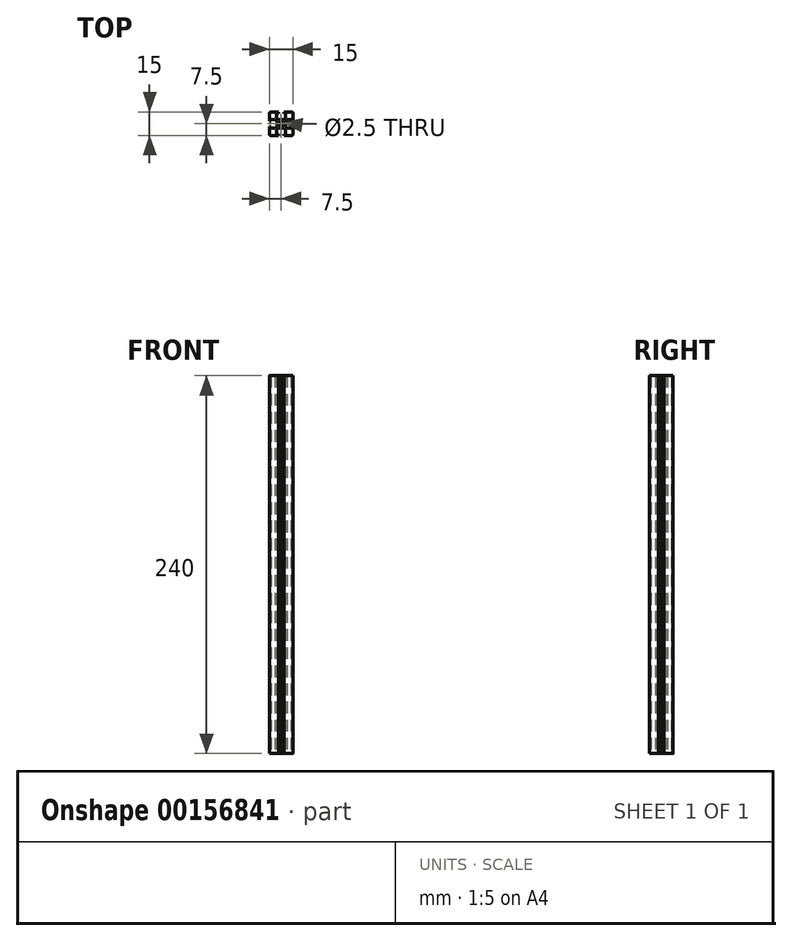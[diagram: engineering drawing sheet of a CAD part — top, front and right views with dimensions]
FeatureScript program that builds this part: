
annotation { "Feature Type Name" : "Feature", "Feature Type Description" : "" }
export const myFeature = defineFeature(function(context is Context, id is Id, definition is map)
    precondition{}
    {
        {
            var Q0;
            Q0=qCreatedBy(makeId("Top.planeOp"),FACE);
            var sketch = newSketch(context, id + "F0", { "sketchPlane" : qUnion([Q0])});
            skLineSegment(sketch, "E0.bottom", {"start": v(6.5, -7.5) * mm, "end": v(1.7, -7.5) * mm});
            skLineSegment(sketch, "E0.top", {"start": v(6.5, 7.5) * mm, "end": v(1.7, 7.5) * mm});
            skLineSegment(sketch, "E0.left", {"start": v(7.5, -6.5) * mm, "end": v(7.5, -1.7) * mm});
            skLineSegment(sketch, "E0.right", {"start": v(-7.5, -6.5) * mm, "end": v(-7.5, -1.7) * mm});
            skPoint(sketch, "E0.middle", {"position": v(0, 0) * mm});
            skPoint(sketch, "E1.visualSharp", {"position": v(7.5, 7.5) * mm});
            skArc(sketch, "E1.filletArc", {"start": v(7.5, 6.5) * mm, "mid": v(7.2, 7.2) * mm, "end": v(6.5, 7.5) * mm});
            skPoint(sketch, "E2.visualSharp", {"position": v(-7.5, 7.5) * mm});
            skArc(sketch, "E2.filletArc", {"start": v(-6.5, 7.5) * mm, "mid": v(-7.2, 7.2) * mm, "end": v(-7.5, 6.5) * mm});
            skPoint(sketch, "E3.visualSharp", {"position": v(-7.5, -7.5) * mm});
            skArc(sketch, "E3.filletArc", {"start": v(-7.5, -6.5) * mm, "mid": v(-7.2, -7.2) * mm, "end": v(-6.5, -7.5) * mm});
            skPoint(sketch, "E4.visualSharp", {"position": v(7.5, -7.5) * mm});
            skArc(sketch, "E4.filletArc", {"start": v(6.5, -7.5) * mm, "mid": v(7.2, -7.2) * mm, "end": v(7.5, -6.5) * mm});
            skCircle(sketch, "E5", {"center": v(0, 0) * mm, "radius": 1.25 * mm});
            skLineSegment(sketch, "E6", {"start": v(-1.7, 7.5) * mm, "end": v(-1.7, 6.4) * mm});
            skLineSegment(sketch, "E7", {"start": v(-1.7, 6.4) * mm, "end": v(-2.85, 6.4) * mm});
            skLineSegment(sketch, "E8", {"start": v(-2.85, 6.4) * mm, "end": v(-2.85, 3.8) * mm});
            skLineSegment(sketch, "E9", {"start": v(-2.85, 3.8) * mm, "end": v(-1.7, 2.8) * mm});
            skLineSegment(sketch, "E10", {"start": v(-1.7, 2.8) * mm, "end": v(-0.52, 2.8) * mm});
            skLineSegment(sketch, "E11", {"start": v(-0.52, 2.8) * mm, "end": v(0, 2.5) * mm});
            skLineSegment(sketch, "E12", {"start": v(0, 7.5) * mm, "end": v(0, 1.25) * mm, "construction": true});
            skLineSegment(sketch, "E13.MirrorCS", {"start": v(1.7, 7.5) * mm, "end": v(1.7, 6.4) * mm});
            skLineSegment(sketch, "E14.MirrorCS", {"start": v(1.7, 6.4) * mm, "end": v(2.85, 6.4) * mm});
            skLineSegment(sketch, "E15.MirrorCS", {"start": v(2.85, 6.4) * mm, "end": v(2.85, 3.8) * mm});
            skLineSegment(sketch, "E16.MirrorCS", {"start": v(2.85, 3.8) * mm, "end": v(1.7, 2.8) * mm});
            skLineSegment(sketch, "E17.MirrorCS", {"start": v(1.7, 2.8) * mm, "end": v(0.52, 2.8) * mm});
            skLineSegment(sketch, "E18.MirrorCS", {"start": v(0.52, 2.8) * mm, "end": v(0, 2.5) * mm});
            skLineSegment(sketch, "E19.1.0", {"start": v(-7.5, -1.7) * mm, "end": v(-6.4, -1.7) * mm});
            skLineSegment(sketch, "E19.1.1", {"start": v(-6.4, -1.7) * mm, "end": v(-6.4, -2.85) * mm});
            skLineSegment(sketch, "E19.1.2", {"start": v(-6.4, -2.85) * mm, "end": v(-3.8, -2.85) * mm});
            skLineSegment(sketch, "E19.1.3", {"start": v(-3.8, -2.85) * mm, "end": v(-2.8, -1.7) * mm});
            skLineSegment(sketch, "E19.1.4", {"start": v(-2.8, -1.7) * mm, "end": v(-2.8, -0.52) * mm});
            skLineSegment(sketch, "E19.1.5", {"start": v(-7.5, 1.7) * mm, "end": v(-6.4, 1.7) * mm});
            skLineSegment(sketch, "E19.1.6", {"start": v(-6.4, 1.7) * mm, "end": v(-6.4, 2.85) * mm});
            skLineSegment(sketch, "E19.1.7", {"start": v(-6.4, 2.85) * mm, "end": v(-3.8, 2.85) * mm});
            skLineSegment(sketch, "E19.1.8", {"start": v(-3.8, 2.85) * mm, "end": v(-2.8, 1.7) * mm});
            skLineSegment(sketch, "E19.1.9", {"start": v(-2.8, 1.7) * mm, "end": v(-2.8, 0.52) * mm});
            skLineSegment(sketch, "E19.1.10", {"start": v(-2.8, 0.52) * mm, "end": v(-2.5, 0) * mm});
            skLineSegment(sketch, "E19.1.11", {"start": v(-2.8, -0.52) * mm, "end": v(-2.5, 0) * mm});
            skLineSegment(sketch, "E19.2.0", {"start": v(1.7, -7.5) * mm, "end": v(1.7, -6.4) * mm});
            skLineSegment(sketch, "E19.2.1", {"start": v(1.7, -6.4) * mm, "end": v(2.85, -6.4) * mm});
            skLineSegment(sketch, "E19.2.2", {"start": v(2.85, -6.4) * mm, "end": v(2.85, -3.8) * mm});
            skLineSegment(sketch, "E19.2.3", {"start": v(2.85, -3.8) * mm, "end": v(1.7, -2.8) * mm});
            skLineSegment(sketch, "E19.2.4", {"start": v(1.7, -2.8) * mm, "end": v(0.52, -2.8) * mm});
            skLineSegment(sketch, "E19.2.5", {"start": v(-1.7, -7.5) * mm, "end": v(-1.7, -6.4) * mm});
            skLineSegment(sketch, "E19.2.6", {"start": v(-1.7, -6.4) * mm, "end": v(-2.85, -6.4) * mm});
            skLineSegment(sketch, "E19.2.7", {"start": v(-2.85, -6.4) * mm, "end": v(-2.85, -3.8) * mm});
            skLineSegment(sketch, "E19.2.8", {"start": v(-2.85, -3.8) * mm, "end": v(-1.7, -2.8) * mm});
            skLineSegment(sketch, "E19.2.9", {"start": v(-1.7, -2.8) * mm, "end": v(-0.52, -2.8) * mm});
            skLineSegment(sketch, "E19.2.10", {"start": v(-0.52, -2.8) * mm, "end": v(0, -2.5) * mm});
            skLineSegment(sketch, "E19.2.11", {"start": v(0.52, -2.8) * mm, "end": v(0, -2.5) * mm});
            skLineSegment(sketch, "E19.3.0", {"start": v(7.5, 1.7) * mm, "end": v(6.4, 1.7) * mm});
            skLineSegment(sketch, "E19.3.1", {"start": v(6.4, 1.7) * mm, "end": v(6.4, 2.85) * mm});
            skLineSegment(sketch, "E19.3.2", {"start": v(6.4, 2.85) * mm, "end": v(3.8, 2.85) * mm});
            skLineSegment(sketch, "E19.3.3", {"start": v(3.8, 2.85) * mm, "end": v(2.8, 1.7) * mm});
            skLineSegment(sketch, "E19.3.4", {"start": v(2.8, 1.7) * mm, "end": v(2.8, 0.52) * mm});
            skLineSegment(sketch, "E19.3.5", {"start": v(7.5, -1.7) * mm, "end": v(6.4, -1.7) * mm});
            skLineSegment(sketch, "E19.3.6", {"start": v(6.4, -1.7) * mm, "end": v(6.4, -2.85) * mm});
            skLineSegment(sketch, "E19.3.7", {"start": v(6.4, -2.85) * mm, "end": v(3.8, -2.85) * mm});
            skLineSegment(sketch, "E19.3.8", {"start": v(3.8, -2.85) * mm, "end": v(2.8, -1.7) * mm});
            skLineSegment(sketch, "E19.3.9", {"start": v(2.8, -1.7) * mm, "end": v(2.8, -0.52) * mm});
            skLineSegment(sketch, "E19.3.10", {"start": v(2.8, -0.52) * mm, "end": v(2.5, 0) * mm});
            skLineSegment(sketch, "E19.3.11", {"start": v(2.8, 0.52) * mm, "end": v(2.5, 0) * mm});
            skLineSegment(sketch, "E20.trimOffspring", {"start": v(-7.5, 1.7) * mm, "end": v(-7.5, 6.5) * mm});
            skLineSegment(sketch, "E21.trimOffspring", {"start": v(-1.7, -7.5) * mm, "end": v(-6.5, -7.5) * mm});
            skLineSegment(sketch, "E22.trimOffspring", {"start": v(7.5, 1.7) * mm, "end": v(7.5, 6.5) * mm});
            skLineSegment(sketch, "E23.trimOffspring", {"start": v(-1.7, 7.5) * mm, "end": v(-6.5, 7.5) * mm});
            skSolve(sketch);
        }
        {
            var Q0;
            Q0=qSketchRegion(id+"F0",true);
            extrude(context, id + "F1", {"entities" : qUnion([Q0]), "endBound" : BoundingType.SYMMETRIC, "depth" : 240 * mm});
        }
    });
